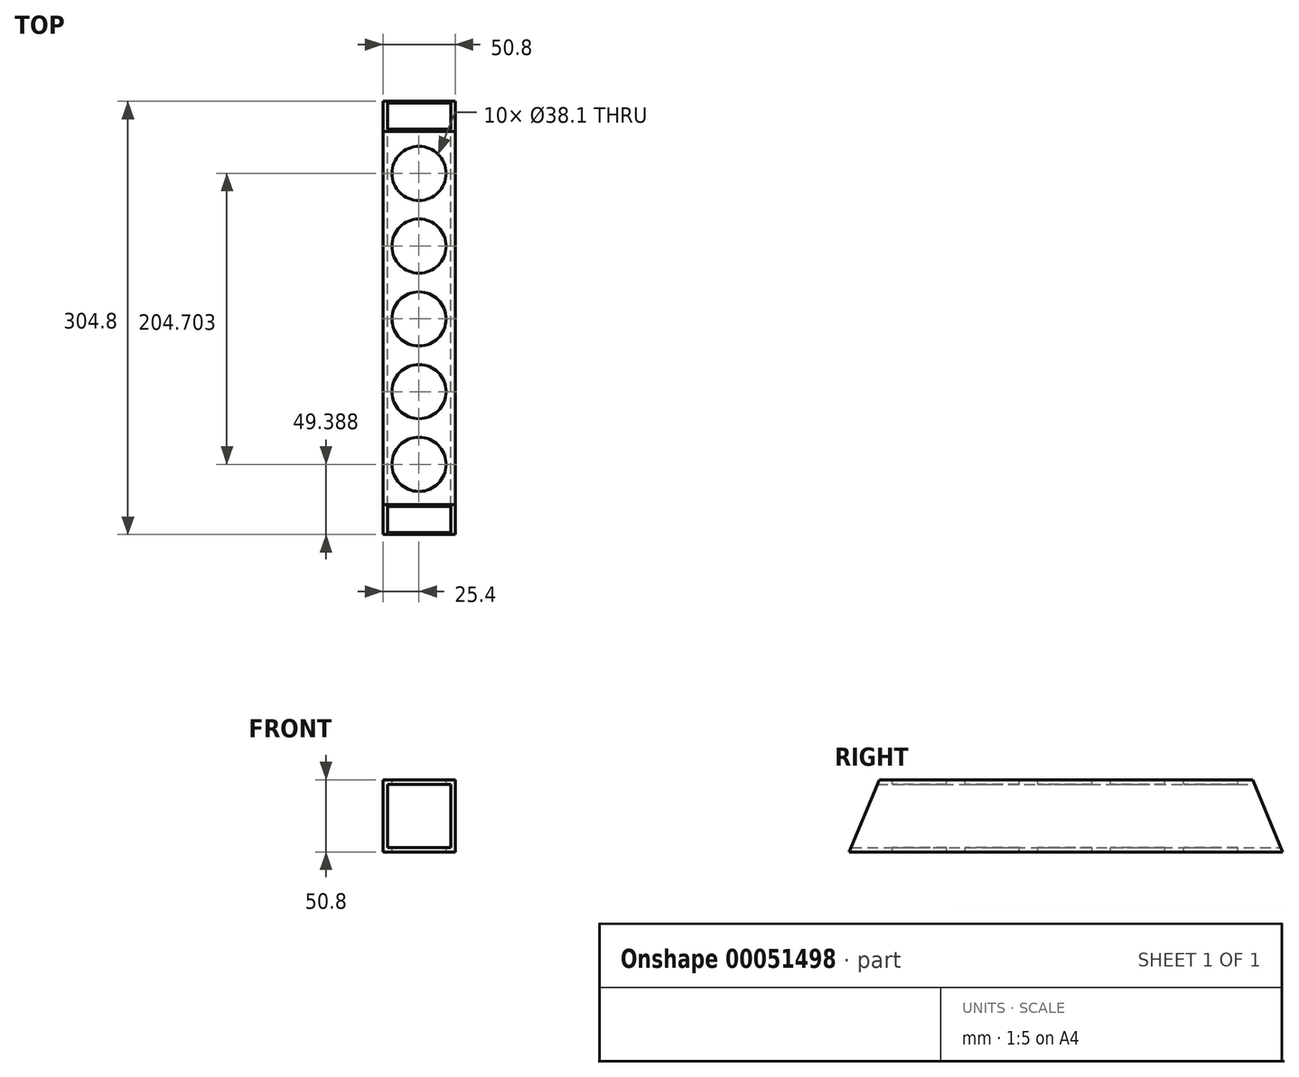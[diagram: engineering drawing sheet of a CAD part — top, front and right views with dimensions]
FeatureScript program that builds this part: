
annotation { "Feature Type Name" : "Feature", "Feature Type Description" : "" }
export const myFeature = defineFeature(function(context is Context, id is Id, definition is map)
    precondition{}
    {
        {
            var Q0;
            Q0=qCreatedBy(makeId("Front.planeOp"),FACE);
            var sketch = newSketch(context, id + "F0", { "sketchPlane" : qUnion([Q0])});
            skLineSegment(sketch, "E0.rect.bottom", {"start": v(25.4, 25.4) * mm, "end": v(-25.4, 25.4) * mm});
            skLineSegment(sketch, "E0.rect.top", {"start": v(25.4, -25.4) * mm, "end": v(-25.4, -25.4) * mm});
            skLineSegment(sketch, "E0.rect.left", {"start": v(25.4, 25.4) * mm, "end": v(25.4, -25.4) * mm});
            skLineSegment(sketch, "E0.rect.right", {"start": v(-25.4, 25.4) * mm, "end": v(-25.4, -25.4) * mm});
            skPoint(sketch, "E0.rect.middle", {"position": v(0, 0) * mm});
            skSolve(sketch);
        }
        {
            var Q0;
            Q0=makeQuery(id+"F0.imprint","IMPRINT",FACE,{"disambiguationData":[TD([[makeQuery(id+"F0.imprint","IMPRINT",EDGE,{"derivedFrom":sQuery(id+"F0.wireOp",EDGE,"E0.rect.bottom")}),1.0]])]});
            var sketch = newSketch(context, id + "F1", { "sketchPlane" : qUnion([Q0])});
            skLineSegment(sketch, "E1.rect.bottom", {"start": v(-22.23, 22.22) * mm, "end": v(22.23, 22.22) * mm});
            skLineSegment(sketch, "E1.rect.top", {"start": v(-22.23, -22.22) * mm, "end": v(22.23, -22.22) * mm});
            skLineSegment(sketch, "E1.rect.left", {"start": v(-22.23, 22.22) * mm, "end": v(-22.23, -22.22) * mm});
            skLineSegment(sketch, "E1.rect.right", {"start": v(22.23, 22.22) * mm, "end": v(22.23, -22.22) * mm});
            skPoint(sketch, "E1.rect.middle", {"position": v(0, 0) * mm});
            skSolve(sketch);
        }
        {
            var Q0;
            Q0=makeQuery(id+"F1.imprint","IMPRINT",FACE,{"disambiguationData":[TD([[makeQuery(id+"F1.imprint","IMPRINT",EDGE,{"derivedFrom":sQuery(id+"F1.wireOp",EDGE,"E1.rect.bottom")}),1.0]])]});
            extrude(context, id + "F2", {"entities" : qUnion([Q0]), "depth" : 304.8 * mm});
        }
        {
            var Q0;
            Q0=makeQuery(id+"F2.opExtrude","SWEPT_FACE",FACE,{"disambiguationData":[OSD([sQuery(id+"F0.wireOp",EDGE,"E0.rect.left")])]});
            var sketch = newSketch(context, id + "F3", { "sketchPlane" : qUnion([Q0])});
            skPoint(sketch, "E2.0.midPoint", {"position": v(-304.8, 25.4) * mm});
            skLineSegment(sketch, "E3", {"start": v(-304.8, 25.4) * mm, "end": v(-304.8, -25.4) * mm});
            skLineSegment(sketch, "E4", {"start": v(-304.8, -25.4) * mm, "end": v(-283.76, 25.4) * mm});
            skLineSegment(sketch, "E5", {"start": v(-283.76, 25.4) * mm, "end": v(-304.8, 25.4) * mm});
            skSolve(sketch);
        }
        {
            var Q0;
            Q0=makeQuery(id+"F3.imprint","IMPRINT",FACE,{"disambiguationData":[TD([[makeQuery(id+"F3.imprint","IMPRINT",EDGE,{"derivedFrom":sQuery(id+"F3.wireOp",EDGE,"E3")}),1.0]])]});
            extrude(context, id + "F4", {"entities" : qUnion([Q0]), "operationType" : NewBodyOperationType.REMOVE, "endBound" : BoundingType.THROUGH_ALL, "oppositeDirection" : true, "depth" : 25.4 * mm});
        }
        {
            var Q0;
            Q0=makeQuery(id+"F2.opExtrude","SWEPT_FACE",FACE,{"disambiguationData":[OSD([sQuery(id+"F0.wireOp",EDGE,"E0.rect.left")])]});
            var sketch = newSketch(context, id + "F5", { "sketchPlane" : qUnion([Q0])});
            skLineSegment(sketch, "E6", {"start": v(0, 25.4) * mm, "end": v(-21.04, 25.4) * mm});
            skLineSegment(sketch, "E7", {"start": v(-21.04, 25.4) * mm, "end": v(0, -25.4) * mm});
            skLineSegment(sketch, "E8", {"start": v(0, -25.4) * mm, "end": v(0, 25.4) * mm});
            skSolve(sketch);
        }
        {
            var Q0;
            Q0=makeQuery(id+"F5.imprint","IMPRINT",FACE,{"disambiguationData":[TD([[makeQuery(id+"F5.imprint","IMPRINT",EDGE,{"derivedFrom":sQuery(id+"F5.wireOp",EDGE,"E6")}),-1.0]])]});
            extrude(context, id + "F6", {"entities" : qUnion([Q0]), "operationType" : NewBodyOperationType.REMOVE, "oppositeDirection" : true, "depth" : 127 * mm});
        }
        {
            var Q0;
            Q0=makeQuery(id+"F2.opExtrude","SWEPT_FACE",FACE,{"disambiguationData":[OSD([sQuery(id+"F0.wireOp",EDGE,"E0.rect.bottom")])]});
            var sketch = newSketch(context, id + "F7", { "sketchPlane" : qUnion([Q0])});
            skCircle(sketch, "E9", {"center": v(0, -50.7) * mm, "radius": 19.05 * mm});
            skCircle(sketch, "E10.1.0.0", {"center": v(0, -101.89) * mm, "radius": 19.05 * mm});
            skCircle(sketch, "E10.2.0.0", {"center": v(0, -153.06) * mm, "radius": 19.05 * mm});
            skCircle(sketch, "E10.3.0.0", {"center": v(0, -204.24) * mm, "radius": 19.05 * mm});
            skCircle(sketch, "E10.4.0.0", {"center": v(0, -255.41) * mm, "radius": 19.05 * mm});
            skLineSegment(sketch, "E10.direction1", {"start": v(0, -50.7) * mm, "end": v(0, -101.89) * mm, "construction": true});
            skSolve(sketch);
        }
        {
            var Q0;
            Q0=makeQuery(id+"F7.imprint","IMPRINT",FACE,{"disambiguationData":[TD([[makeQuery(id+"F7.imprint","IMPRINT",EDGE,{"derivedFrom":sQuery(id+"F7.wireOp",EDGE,"E9")}),1.0]])]});
            var Q1;
            Q1=makeQuery(id+"F7.imprint","IMPRINT",FACE,{"disambiguationData":[TD([[makeQuery(id+"F7.imprint","IMPRINT",EDGE,{"derivedFrom":sQuery(id+"F7.wireOp",EDGE,"E10.1.0.0")}),1.0]])]});
            var Q2;
            Q2=makeQuery(id+"F7.imprint","IMPRINT",FACE,{"disambiguationData":[TD([[makeQuery(id+"F7.imprint","IMPRINT",EDGE,{"derivedFrom":sQuery(id+"F7.wireOp",EDGE,"E10.2.0.0")}),1.0]])]});
            var Q3;
            Q3=makeQuery(id+"F7.imprint","IMPRINT",FACE,{"disambiguationData":[TD([[makeQuery(id+"F7.imprint","IMPRINT",EDGE,{"derivedFrom":sQuery(id+"F7.wireOp",EDGE,"E10.3.0.0")}),1.0]])]});
            var Q4;
            Q4=makeQuery(id+"F7.imprint","IMPRINT",FACE,{"disambiguationData":[TD([[makeQuery(id+"F7.imprint","IMPRINT",EDGE,{"derivedFrom":sQuery(id+"F7.wireOp",EDGE,"E10.4.0.0")}),1.0]])]});
            extrude(context, id + "F8", {"entities" : qUnion([Q0, Q1, Q2, Q3, Q4]), "operationType" : NewBodyOperationType.REMOVE, "oppositeDirection" : true, "depth" : 50.8 * mm});
        }
    });
